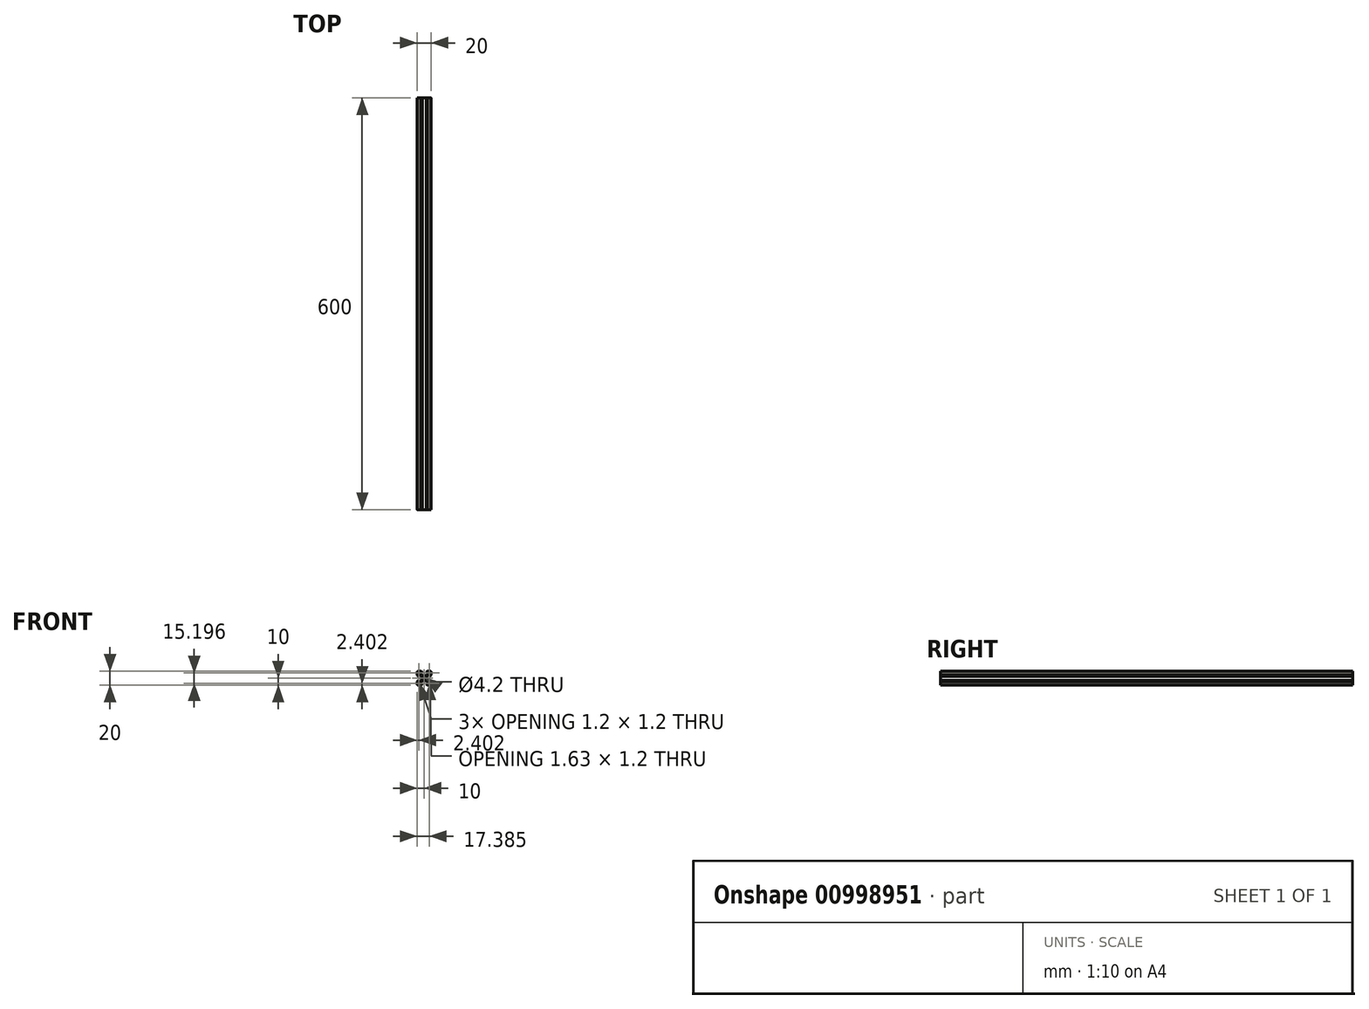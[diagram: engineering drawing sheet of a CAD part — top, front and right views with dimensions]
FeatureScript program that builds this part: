
annotation { "Feature Type Name" : "Feature", "Feature Type Description" : "" }
export const myFeature = defineFeature(function(context is Context, id is Id, definition is map)
    precondition{}
    {
        {
            assignVariable(context, id + "F0", {"name" : "ExtrusionLength", "anyValue" : 600});
        }
        {
            var Q0;
            Q0=qCreatedBy(makeId("Front.planeOp"),FACE);
            var sketch = newSketch(context, id + "F1", { "sketchPlane" : qUnion([Q0])});
            skLineSegment(sketch, "E0.bottom", {"start": v(10, 10) * mm, "end": v(-10, 10) * mm});
            skLineSegment(sketch, "E0.top", {"start": v(10, -10) * mm, "end": v(-10, -10) * mm});
            skLineSegment(sketch, "E0.left", {"start": v(10, 10) * mm, "end": v(10, -10) * mm});
            skLineSegment(sketch, "E0.right", {"start": v(-10, 10) * mm, "end": v(-10, -10) * mm});
            skPoint(sketch, "E0.middle", {"position": v(0, 0) * mm});
            skCircle(sketch, "E1", {"center": v(0, 0) * mm, "radius": 2.1 * mm});
            skLineSegment(sketch, "E2", {"start": v(0, 0) * mm, "end": v(10, 10) * mm, "construction": true});
            skLineSegment(sketch, "E3", {"start": v(0, 0) * mm, "end": v(-0.53, 0.53) * mm});
            skLineSegment(sketch, "E4", {"start": v(-0.53, 0.53) * mm, "end": v(5.5, 6.56) * mm});
            skLineSegment(sketch, "E5.MirrorCS", {"start": v(0.53, -0.53) * mm, "end": v(6.56, 5.5) * mm});
            skLineSegment(sketch, "E6.MirrorCS", {"start": v(0, 0) * mm, "end": v(0.53, -0.53) * mm});
            skLineSegment(sketch, "E7.0", {"start": v(8.2, 8.2) * mm, "end": v(6.57, 8.2) * mm});
            skLineSegment(sketch, "E7.1", {"start": v(8.2, 8.2) * mm, "end": v(8.2, 6.57) * mm});
            skLineSegment(sketch, "E7.2", {"start": v(8.2, -8.2) * mm, "end": v(6.57, -8.2) * mm});
            skLineSegment(sketch, "E7.3", {"start": v(-8.2, 8.2) * mm, "end": v(-8.2, 6.57) * mm});
            skLineSegment(sketch, "E8", {"start": v(4.64, 10) * mm, "end": v(0, 5.36) * mm});
            skLineSegment(sketch, "E9", {"start": v(0, 5.36) * mm, "end": v(-4.64, 10) * mm});
            skLineSegment(sketch, "E10", {"start": v(5.5, 8.2) * mm, "end": v(5.5, 6.56) * mm});
            skLineSegment(sketch, "E11.MirrorCS", {"start": v(8.2, 5.5) * mm, "end": v(6.56, 5.5) * mm});
            skLineSegment(sketch, "E12", {"start": v(6.57, 8.2) * mm, "end": v(8.2, 6.57) * mm});
            skLineSegment(sketch, "E13", {"start": v(0, 0) * mm, "end": v(0, -3.2) * mm, "construction": true});
            skLineSegment(sketch, "E14", {"start": v(0, 0) * mm, "end": v(-2.46, 0) * mm, "construction": true});
            skLineSegment(sketch, "E15", {"start": v(5.5, 6.56) * mm, "end": v(8.94, 10) * mm, "construction": true});
            skLineSegment(sketch, "E16", {"start": v(6.56, 5.5) * mm, "end": v(10, 8.94) * mm, "construction": true});
            skLineSegment(sketch, "E17", {"start": v(8.2, 6.57) * mm, "end": v(8.2, 5.5) * mm, "construction": true});
            skLineSegment(sketch, "E18", {"start": v(8.2, 5.5) * mm, "end": v(8.2, -5.5) * mm});
            skLineSegment(sketch, "E19", {"start": v(5.5, 8.2) * mm, "end": v(-8.2, 8.2) * mm});
            skLineSegment(sketch, "E20", {"start": v(6.57, 8.2) * mm, "end": v(5.5, 8.2) * mm, "construction": true});
            skLineSegment(sketch, "E21.MirrorCS", {"start": v(-0.53, -0.53) * mm, "end": v(5.5, -6.56) * mm});
            skLineSegment(sketch, "E22.MirrorCS", {"start": v(0.53, 0.53) * mm, "end": v(6.56, -5.5) * mm});
            skLineSegment(sketch, "E23.MirrorCS", {"start": v(8.2, -5.5) * mm, "end": v(6.56, -5.5) * mm});
            skLineSegment(sketch, "E24.MirrorCS", {"start": v(5.5, -8.2) * mm, "end": v(5.5, -6.56) * mm});
            skLineSegment(sketch, "E25.MirrorCS", {"start": v(6.57, -8.2) * mm, "end": v(8.2, -6.57) * mm});
            skLineSegment(sketch, "E26.MirrorCS", {"start": v(4.64, -10) * mm, "end": v(0, -5.36) * mm});
            skLineSegment(sketch, "E27.MirrorCS", {"start": v(0, -5.36) * mm, "end": v(-4.64, -10) * mm});
            skLineSegment(sketch, "E28.MirrorCS", {"start": v(0.53, -0.53) * mm, "end": v(-5.5, -6.56) * mm});
            skLineSegment(sketch, "E29.MirrorCS", {"start": v(-0.53, 0.53) * mm, "end": v(-6.56, -5.5) * mm});
            skLineSegment(sketch, "E30.MirrorCS", {"start": v(-8.2, -5.5) * mm, "end": v(-6.56, -5.5) * mm});
            skLineSegment(sketch, "E31.MirrorCS", {"start": v(-6.57, -8.2) * mm, "end": v(-8.2, -6.57) * mm});
            skLineSegment(sketch, "E32.MirrorCS", {"start": v(-5.5, -8.2) * mm, "end": v(-5.5, -6.56) * mm});
            skLineSegment(sketch, "E33.MirrorCS", {"start": v(-0.53, -0.53) * mm, "end": v(-6.56, 5.5) * mm});
            skLineSegment(sketch, "E34.MirrorCS", {"start": v(0.53, 0.53) * mm, "end": v(-5.5, 6.56) * mm});
            skLineSegment(sketch, "E35.MirrorCS", {"start": v(-8.2, 5.5) * mm, "end": v(-6.56, 5.5) * mm});
            skLineSegment(sketch, "E36.MirrorCS", {"start": v(-5.5, 8.2) * mm, "end": v(-5.5, 6.56) * mm});
            skLineSegment(sketch, "E37.MirrorCS", {"start": v(-6.57, 8.2) * mm, "end": v(-8.2, 6.57) * mm});
            skLineSegment(sketch, "E38", {"start": v(8.2, -5.5) * mm, "end": v(8.2, -6.57) * mm, "construction": true});
            skLineSegment(sketch, "E39", {"start": v(8.2, -6.57) * mm, "end": v(8.2, -8.2) * mm});
            skLineSegment(sketch, "E40", {"start": v(6.57, -8.2) * mm, "end": v(5.5, -8.2) * mm, "construction": true});
            skLineSegment(sketch, "E41", {"start": v(5.5, -8.2) * mm, "end": v(-5.5, -8.2) * mm});
            skLineSegment(sketch, "E42", {"start": v(-6.57, -8.2) * mm, "end": v(-8.2, -8.2) * mm});
            skLineSegment(sketch, "E43", {"start": v(-5.5, -8.2) * mm, "end": v(-6.57, -8.2) * mm, "construction": true});
            skLineSegment(sketch, "E44", {"start": v(-8.2, -6.57) * mm, "end": v(-8.2, -8.2) * mm});
            skLineSegment(sketch, "E45", {"start": v(-8.2, -5.5) * mm, "end": v(-8.2, -6.57) * mm, "construction": true});
            skLineSegment(sketch, "E46", {"start": v(-8.2, 6.57) * mm, "end": v(-8.2, 5.5) * mm, "construction": true});
            skLineSegment(sketch, "E47", {"start": v(-8.2, 5.5) * mm, "end": v(-8.2, -5.5) * mm});
            skLineSegment(sketch, "E48", {"start": v(3.9, 2.84) * mm, "end": v(3.9, -2.84) * mm});
            skLineSegment(sketch, "E49", {"start": v(2.84, 3.9) * mm, "end": v(-2.84, 3.9) * mm});
            skLineSegment(sketch, "E50", {"start": v(-3.9, 2.84) * mm, "end": v(-3.9, -2.84) * mm});
            skLineSegment(sketch, "E51", {"start": v(-2.84, -3.9) * mm, "end": v(2.84, -3.9) * mm});
            skPoint(sketch, "E52", {"position": v(-2.84, 8.2) * mm});
            skPoint(sketch, "E53", {"position": v(2.84, 8.2) * mm});
            skPoint(sketch, "E54", {"position": v(2.84, -8.2) * mm});
            skPoint(sketch, "E55", {"position": v(-2.84, -8.2) * mm});
            skLineSegment(sketch, "E56", {"start": v(-10, 4.64) * mm, "end": v(-5.36, 0) * mm});
            skLineSegment(sketch, "E57", {"start": v(-5.36, 0) * mm, "end": v(-10, -4.64) * mm});
            skPoint(sketch, "E58", {"position": v(-8.2, 2.84) * mm});
            skPoint(sketch, "E59", {"position": v(-8.2, -2.84) * mm});
            skLineSegment(sketch, "E60.MirrorCS", {"start": v(5.36, 0) * mm, "end": v(10, -4.64) * mm});
            skLineSegment(sketch, "E61.MirrorCS", {"start": v(10, 4.64) * mm, "end": v(5.36, 0) * mm});
            skPoint(sketch, "E62.MirrorP", {"position": v(8.2, 2.84) * mm});
            skPoint(sketch, "E63.MirrorP", {"position": v(8.2, -2.84) * mm});
            skSolve(sketch);
        }
        {
            var Q0;
            {var subQ17=sQuery(id+"F1.wireOp",EDGE,"E7.3");Q0=makeQuery(id+"F1.imprint","IMPRINT",FACE,{"disambiguationData":[TD([[makeQuery(id+"F1.imprint","IMPRINT",EDGE,{"derivedFrom":subQ17}),-1.0]])]});}
            var Q1;
            {var subQ5=sQuery(id+"F1.wireOp",EDGE,"E49");Q1=makeQuery(id+"F1.imprint","IMPRINT",FACE,{"disambiguationData":[TD([[makeQuery(id+"F1.imprint","IMPRINT",EDGE,{"derivedFrom":subQ5}),1.0]])]});}
            var Q2;
            {var subQ5=sQuery(id+"F1.wireOp",EDGE,"E48");Q2=makeQuery(id+"F1.imprint","IMPRINT",FACE,{"disambiguationData":[TD([[makeQuery(id+"F1.imprint","IMPRINT",EDGE,{"derivedFrom":subQ5}),-1.0]])]});}
            var Q3;
            Q3=makeQuery(id+"F1.imprint","IMPRINT",FACE,{"disambiguationData":[TD([[makeQuery(id+"F1.imprint","IMPRINT",EDGE,{"derivedFrom":sQuery(id+"F1.wireOp",EDGE,"E7.0")}),-1.0]])]});
            var Q4;
            {var subQ5=sQuery(id+"F1.wireOp",EDGE,"E50");Q4=makeQuery(id+"F1.imprint","IMPRINT",FACE,{"disambiguationData":[TD([[makeQuery(id+"F1.imprint","IMPRINT",EDGE,{"derivedFrom":subQ5}),1.0]])]});}
            var Q5;
            {var subQ0=sQuery(id+"F1.wireOp",EDGE,"E30.MirrorCS");Q5=makeQuery(id+"F1.imprint","IMPRINT",FACE,{"disambiguationData":[TD([[makeQuery(id+"F1.imprint","IMPRINT",EDGE,{"derivedFrom":subQ0}),-1.0]])]});}
            var Q6;
            Q6=makeQuery(id+"F1.imprint","IMPRINT",FACE,{"disambiguationData":[TD([[makeQuery(id+"F1.imprint","IMPRINT",EDGE,{"derivedFrom":sQuery(id+"F1.wireOp",EDGE,"E7.2")}),1.0]])]});
            var Q7;
            {var subQ5=sQuery(id+"F1.wireOp",EDGE,"E51");Q7=makeQuery(id+"F1.imprint","IMPRINT",FACE,{"disambiguationData":[TD([[makeQuery(id+"F1.imprint","IMPRINT",EDGE,{"derivedFrom":subQ5}),1.0]])]});}
            extrude(context, id + "F2", {"entities" : qUnion([Q0, Q1, Q2, Q3, Q4, Q5, Q6, Q7]), "oppositeDirection" : true, "depth" : (getVariable(context, 'ExtrusionLength')) * mm, "offsetDistance" : 25 * mm});
        }
        {
            var Q0;
            Q0=makeQuery(id+"F2.opExtrude","SWEPT_EDGE",EDGE,{"disambiguationData":[OSD([sQuery(id+"F1.wireOp",EDGE,"E0.bottom"),sQuery(id+"F1.wireOp",EDGE,"E0.left")])]});
            var Q1;
            Q1=makeQuery(id+"F2.opExtrude","SWEPT_EDGE",EDGE,{"disambiguationData":[OSD([sQuery(id+"F1.wireOp",EDGE,"E0.top"),sQuery(id+"F1.wireOp",EDGE,"E0.left")])]});
            var Q2;
            Q2=makeQuery(id+"F2.opExtrude","SWEPT_EDGE",EDGE,{"disambiguationData":[OSD([sQuery(id+"F1.wireOp",EDGE,"E0.bottom"),sQuery(id+"F1.wireOp",EDGE,"E0.right")])]});
            var Q3;
            Q3=makeQuery(id+"F2.opExtrude","SWEPT_EDGE",EDGE,{"disambiguationData":[OSD([sQuery(id+"F1.wireOp",EDGE,"E0.top"),sQuery(id+"F1.wireOp",EDGE,"E0.right")])]});
            fillet(context, id + "F3", {"entities" : qUnion([Q0, Q1, Q2, Q3]), "radius" : 1 * mm, "tangentPropagation" : true, "allowEdgeOverflow" : false});
        }
        {
            var Q0;
            Q0=makeQuery(id+"F2.opExtrude","SWEPT_EDGE",EDGE,{"disambiguationData":[OSD([sQuery(id+"F1.wireOp",EDGE,"E7.3"),sQuery(id+"F1.wireOp",EDGE,"E37.MirrorCS")])]});
            var Q1;
            Q1=makeQuery(id+"F2.opExtrude","SWEPT_EDGE",EDGE,{"disambiguationData":[OSD([sQuery(id+"F1.wireOp",EDGE,"E19"),sQuery(id+"F1.wireOp",EDGE,"E37.MirrorCS")])]});
            var Q2;
            Q2=makeQuery(id+"F2.opExtrude","SWEPT_EDGE",EDGE,{"disambiguationData":[OSD([sQuery(id+"F1.wireOp",EDGE,"E7.0"),sQuery(id+"F1.wireOp",EDGE,"E12")])]});
            var Q3;
            Q3=makeQuery(id+"F2.opExtrude","SWEPT_EDGE",EDGE,{"disambiguationData":[OSD([sQuery(id+"F1.wireOp",EDGE,"E7.1"),sQuery(id+"F1.wireOp",EDGE,"E12")])]});
            var Q4;
            Q4=makeQuery(id+"F2.opExtrude","SWEPT_EDGE",EDGE,{"disambiguationData":[OSD([sQuery(id+"F1.wireOp",EDGE,"E7.2"),sQuery(id+"F1.wireOp",EDGE,"E39")])]});
            var Q5;
            Q5=makeQuery(id+"F2.opExtrude","SWEPT_EDGE",EDGE,{"disambiguationData":[OSD([sQuery(id+"F1.wireOp",EDGE,"E31.MirrorCS"),sQuery(id+"F1.wireOp",EDGE,"E42")])]});
            var Q6;
            Q6=makeQuery(id+"F2.opExtrude","SWEPT_EDGE",EDGE,{"disambiguationData":[OSD([sQuery(id+"F1.wireOp",EDGE,"E31.MirrorCS"),sQuery(id+"F1.wireOp",EDGE,"E44")])]});
            var Q7;
            Q7=makeQuery(id+"F2.opExtrude","SWEPT_EDGE",EDGE,{"disambiguationData":[OSD([sQuery(id+"F1.wireOp",EDGE,"E25.MirrorCS"),sQuery(id+"F1.wireOp",EDGE,"E39")])]});
            chamfer(context, id + "F4", {"entities" : qUnion([Q0, Q1, Q2, Q3, Q4, Q5, Q6, Q7]), "width" : .25 * mm, "tangentPropagation" : true});
        }
    });
